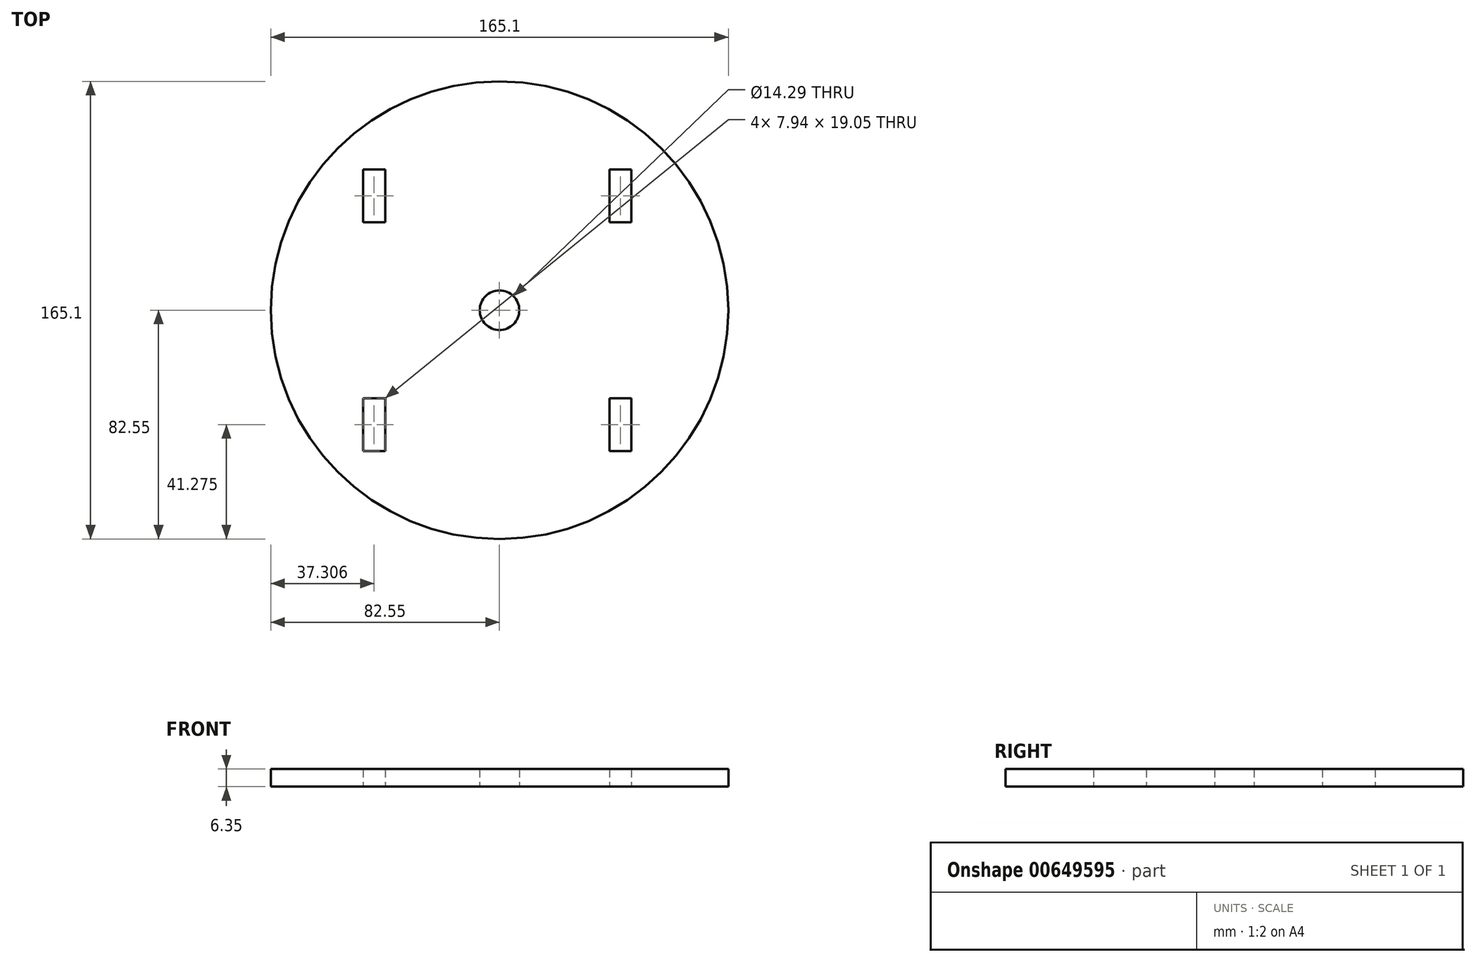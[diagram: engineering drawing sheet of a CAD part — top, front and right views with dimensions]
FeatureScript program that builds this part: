
annotation { "Feature Type Name" : "Feature", "Feature Type Description" : "" }
export const myFeature = defineFeature(function(context is Context, id is Id, definition is map)
    precondition{}
    {
        {
            var Q0;
            Q0=qCreatedBy(makeId("Top.planeOp"),FACE);
            var sketch = newSketch(context, id + "F0", { "sketchPlane" : qUnion([Q0])});
            skCircle(sketch, "E0", {"center": v(0, 0) * mm, "radius": 82.55 * mm});
            skCircle(sketch, "E1", {"center": v(0, 0) * mm, "radius": 7.14 * mm});
            skLineSegment(sketch, "E2", {"start": v(82.55, 0) * mm, "end": v(44.45, 0) * mm, "construction": true});
            skLineSegment(sketch, "E3", {"start": v(44.45, 69.56) * mm, "end": v(44.45, -69.56) * mm, "construction": true});
            skLineSegment(sketch, "E4", {"start": v(-44.45, -69.56) * mm, "end": v(-44.45, 69.56) * mm, "construction": true});
            skLineSegment(sketch, "E5", {"start": v(-49.21, 31.75) * mm, "end": v(-41.28, 31.75) * mm});
            skLineSegment(sketch, "E6", {"start": v(-49.21, 50.8) * mm, "end": v(-41.28, 50.8) * mm});
            skLineSegment(sketch, "E7", {"start": v(-41.28, 50.8) * mm, "end": v(-41.28, 31.75) * mm});
            skLineSegment(sketch, "E8", {"start": v(-49.21, 31.75) * mm, "end": v(-49.21, 50.8) * mm});
            skLineSegment(sketch, "E9", {"start": v(-49.21, -31.75) * mm, "end": v(-41.28, -31.75) * mm});
            skLineSegment(sketch, "E10", {"start": v(-41.28, -31.75) * mm, "end": v(-41.28, -50.8) * mm});
            skLineSegment(sketch, "E11", {"start": v(-41.28, -50.8) * mm, "end": v(-49.21, -50.8) * mm});
            skLineSegment(sketch, "E12", {"start": v(-49.21, -50.8) * mm, "end": v(-49.21, -31.75) * mm});
            skLineSegment(sketch, "E13", {"start": v(47.62, 50.8) * mm, "end": v(39.69, 50.8) * mm});
            skLineSegment(sketch, "E14", {"start": v(39.69, 50.8) * mm, "end": v(39.69, 31.75) * mm});
            skLineSegment(sketch, "E15", {"start": v(39.69, 31.75) * mm, "end": v(47.62, 31.75) * mm});
            skLineSegment(sketch, "E16", {"start": v(47.62, 31.75) * mm, "end": v(47.62, 50.8) * mm});
            skLineSegment(sketch, "E17", {"start": v(47.63, -31.75) * mm, "end": v(39.69, -31.75) * mm});
            skLineSegment(sketch, "E18", {"start": v(39.69, -31.75) * mm, "end": v(39.69, -50.8) * mm});
            skLineSegment(sketch, "E19", {"start": v(39.69, -50.8) * mm, "end": v(47.63, -50.8) * mm});
            skLineSegment(sketch, "E20", {"start": v(47.63, -50.8) * mm, "end": v(47.63, -31.75) * mm});
            skLineSegment(sketch, "E21", {"start": v(-44.45, 41.27) * mm, "end": v(-47.62, 41.27) * mm, "construction": true});
            skPoint(sketch, "E21.startSnap0", {"position": v(-41.28, 41.27) * mm});
            skLineSegment(sketch, "E22", {"start": v(44.45, 41.28) * mm, "end": v(41.27, 41.28) * mm, "construction": true});
            skPoint(sketch, "E22.startSnap0", {"position": v(47.62, 41.28) * mm});
            skSolve(sketch);
        }
        {
            var Q0;
            Q0=makeQuery(id+"F0.imprint","IMPRINT",FACE,{"disambiguationData":[TD([[makeQuery(id+"F0.imprint","IMPRINT",EDGE,{"derivedFrom":sQuery(id+"F0.wireOp",EDGE,"E0")}),1.0]])]});
            extrude(context, id + "F1", {"entities" : qUnion([Q0]), "depth" : 6.35 * mm, "offsetDistance" : 25.4 * mm});
        }
    });
